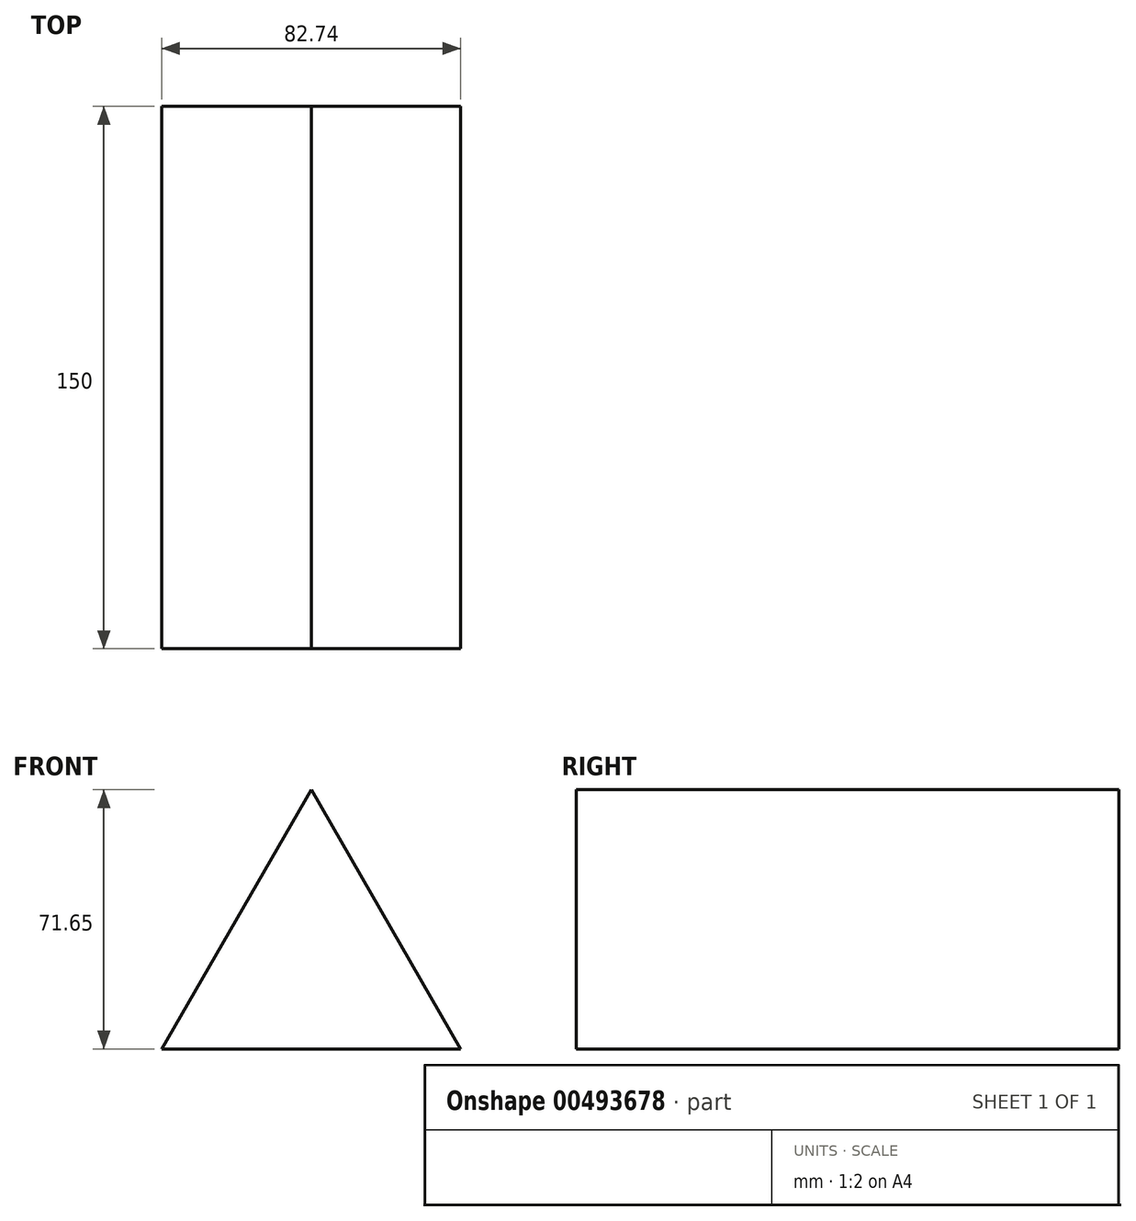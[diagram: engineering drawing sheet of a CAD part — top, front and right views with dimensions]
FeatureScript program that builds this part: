
annotation { "Feature Type Name" : "Feature", "Feature Type Description" : "" }
export const myFeature = defineFeature(function(context is Context, id is Id, definition is map)
    precondition{}
    {
        {
            var Q0;
            Q0=qCreatedBy(makeId("Front.planeOp"),FACE);
            var sketch = newSketch(context, id + "F0", { "sketchPlane" : qUnion([Q0])});
            skCircle(sketch, "E0.cCircle", {"center": v(0, 0) * mm, "radius": 47.77 * mm, "construction": true});
            skLineSegment(sketch, "E0.0", {"start": v(0, 47.77) * mm, "end": v(41.37, -23.88) * mm});
            skLineSegment(sketch, "E0.1", {"start": v(41.37, -23.88) * mm, "end": v(-41.37, -23.88) * mm});
            skLineSegment(sketch, "E0.2", {"start": v(-41.37, -23.88) * mm, "end": v(0, 47.77) * mm});
            skSolve(sketch);
        }
        {
            var Q0;
            Q0=makeQuery(id+"F0.imprint","IMPRINT",FACE,{"disambiguationData":[TD([[makeQuery(id+"F0.imprint","IMPRINT",EDGE,{"derivedFrom":sQuery(id+"F0.wireOp",EDGE,"E0.0")}),-1.0]])]});
            extrude(context, id + "F1", {"entities" : qUnion([Q0]), "depth" : 150 * mm});
        }
    });
